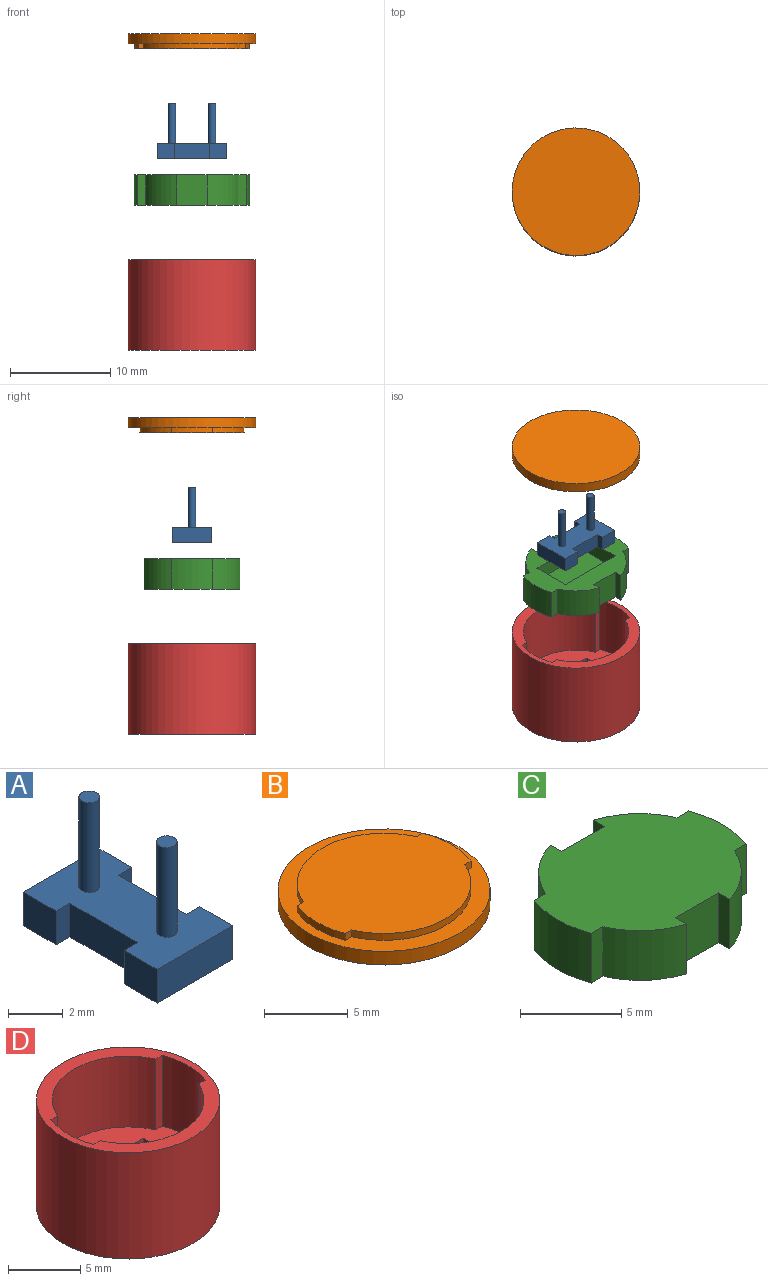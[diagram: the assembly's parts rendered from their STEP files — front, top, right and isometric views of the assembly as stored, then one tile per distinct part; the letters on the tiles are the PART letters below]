
ASSEMBLY  parts=4 mates=3
PART A: 18 faces, bbox 3.9x6.9x5.5 mm
  f0: plane 1.7x1.5mm, normal (1,0,0), area 2.5mm2, adj f2,f4,f7,f17
  f1: plane 1.7x1.5mm, normal (-1,0,0), area 2.5mm2, adj f2,f4,f7,f12
  f2: plane 6.9x3.9mm, normal (0,0,-1), area 22mm2, adj f0,f1,f3,f4,f5,f6,f12,f13
  f3: plane 1.7x1.5mm, normal (1,0,0), area 2.5mm2, adj f2,f6,f7,f15
  f4: plane 3.9x1.5mm, normal (0,1,0), area 5.9mm2, adj f0,f1,f2,f7
  f5: plane 1.7x1.5mm, normal (-1,0,0), area 2.5mm2, adj f2,f6,f7,f14
  f6: plane 3.9x1.5mm, normal (0,-1,0), area 5.9mm2, adj f2,f3,f5,f7
  f7: plane 6.9x3.9mm, normal (0,0,1), area 21.1mm2, adj f0,f1,f3,f4,f5,f6,f8,f10
  f8: cylinder r=0.38mm len=4mm, axis (0,0,-1), area 9.4mm2, adj f7,f9
  f9: plane 0.75x0.75mm, normal (0,0,1), area 0.4mm2, adj f8
  f10: cylinder r=0.38mm len=4mm, axis (0,0,-1), area 9.4mm2, adj f7,f11
  f11: plane 0.75x0.75mm, normal (0,0,1), area 0.4mm2, adj f10
  f12: plane 1.5x0.7mm, normal (0,-1,0), area 1.1mm2, adj f1,f2,f7,f13
  f13: plane 3.5x1.5mm, normal (-1,0,0), area 5.2mm2, adj f2,f7,f12,f14
  f14: plane 1.5x0.7mm, normal (0,1,0), area 1.1mm2, adj f2,f5,f7,f13
  f15: plane 1.5x0.7mm, normal (0,1,0), area 1.1mm2, adj f2,f3,f7,f16
  f16: plane 3.5x1.5mm, normal (1,0,0), area 5.2mm2, adj f2,f7,f15,f17
  f17: plane 1.5x0.7mm, normal (0,-1,0), area 1.1mm2, adj f0,f2,f7,f16
PART B: 12 faces, bbox 12.7x12.7x1.5 mm
  f0: cylinder r=6.35mm len=12.7mm, axis (0,0,1), area 39.9mm2, adj f1,f2
  f1: plane 12.7x12.7mm, normal (0,0,-1), area 126.7mm2, adj f0
  f2: plane 12.7x12.7mm, normal (0,0,1), area 37.5mm2, adj f0,f4,f5,f6,f7,f8,f9,f10
  f3: plane 11.4x10.4mm, normal (0,0,1), area 89.2mm2, adj f4,f5,f6,f7,f8,f9,f10,f11
  f4: plane 0.54x0.5mm, normal (0,1,0), area 0.3mm2, adj f2,f3,f6,f11
  f5: plane 0.54x0.5mm, normal (0,-1,0), area 0.3mm2, adj f2,f3,f6,f10
  f6: cylinder r=5.7mm len=4.1mm, axis (0,0,1), area 2.1mm2, adj f2,f3,f4,f5
  f7: plane 0.54x0.5mm, normal (0,-1,0), area 0.3mm2, adj f2,f3,f8,f10
  f8: cylinder r=5.7mm len=4.1mm, axis (0,0,1), area 2.1mm2, adj f2,f3,f7,f9
  f9: plane 0.54x0.5mm, normal (0,1,0), area 0.3mm2, adj f2,f3,f8,f11
  f10: cylinder r=5.2mm len=9.56mm, axis (0,0,1), area 6.1mm2, adj f2,f3,f5,f7
  f11: cylinder r=5.2mm len=9.56mm, axis (0,0,1), area 6.1mm2, adj f2,f3,f4,f9
PART C: 23 faces, bbox 11.5x9.5x3 mm
  f0: plane 11.5x9.54mm, normal (0,0,-1), area 51.1mm2, adj f1,f2,f4,f5,f6,f7,f8,f9
  f1: cylinder r=5mm len=3.08mm, axis (0,0,1), area 12.8mm2, adj f0,f3,f10,f18
  f2: cylinder r=5mm len=3.08mm, axis (0,0,1), area 12.8mm2, adj f0,f3,f8,f22
  f3: plane 11.5x9.54mm, normal (0,0,1), area 79.1mm2, adj f1,f2,f4,f5,f6,f7,f8,f9
  f4: cylinder r=5mm len=3.08mm, axis (0,0,1), area 12.8mm2, adj f0,f3,f7,f19
  f5: cylinder r=5mm len=3.08mm, axis (0,0,1), area 12.8mm2, adj f0,f3,f9,f20
  f6: cylinder r=5.75mm len=4mm, axis (0,0,1), area 12.3mm2, adj f0,f3,f7,f8
  f7: plane 3x0.81mm, normal (0,-1,0), area 2.4mm2, adj f0,f3,f4,f6
  f8: plane 3x0.81mm, normal (0,1,0), area 2.4mm2, adj f0,f2,f3,f6
  f9: plane 3x0.81mm, normal (0,1,0), area 2.4mm2, adj f0,f3,f5,f11
  f10: plane 3x0.81mm, normal (0,-1,0), area 2.4mm2, adj f0,f1,f3,f11
  f11: cylinder r=5.75mm len=4mm, axis (0,0,1), area 12.3mm2, adj f0,f3,f9,f10
  f12: plane 4x1.5mm, normal (-1,0,0), area 6mm2, adj f0,f13,f15,f16
  f13: plane 7x1.5mm, normal (0,1,0), area 10.5mm2, adj f0,f12,f14,f16
  f14: plane 4x1.5mm, normal (1,0,0), area 6mm2, adj f0,f13,f15,f16
  f15: plane 7x1.5mm, normal (0,-1,0), area 10.5mm2, adj f0,f12,f14,f16
  f16: plane 7x4mm, normal (0,0,-1), area 28mm2, adj f12,f13,f14,f15
  f17: plane 3x3mm, normal (0,-1,0), area 9mm2, adj f0,f3,f18,f19
  f18: plane 3x0.77mm, normal (-1,0,0), area 2.3mm2, adj f0,f1,f3,f17
  f19: plane 3x0.77mm, normal (1,0,0), area 2.3mm2, adj f0,f3,f4,f17
  f20: plane 3x0.77mm, normal (-1,0,0), area 2.3mm2, adj f0,f3,f5,f21
  f21: plane 3x3mm, normal (0,1,0), area 9mm2, adj f0,f3,f20,f22
  f22: plane 3x0.77mm, normal (1,0,0), area 2.3mm2, adj f0,f2,f3,f21
PART D: 17 faces, bbox 12.7x12.7x9 mm
  f0: plane 11.7x10.5mm, normal (0,0,1), area 63.8mm2, adj f1,f2,f6,f7,f8,f9,f10,f11
  f1: cylinder r=5.25mm len=9.62mm, axis (0,0,1), area 73mm2, adj f0,f4,f6,f9
  f2: cylinder r=5.25mm len=9.62mm, axis (0,0,1), area 73mm2, adj f0,f4,f8,f11
  f3: cylinder r=6.35mm len=12.7mm, axis (0,0,-1), area 359.1mm2, adj f4,f5
  f4: plane 12.7x12.7mm, normal (0,0,1), area 34.9mm2, adj f1,f2,f3,f6,f7,f8,f9,f10
  f5: plane 12.7x12.7mm, normal (0,0,-1), area 126.7mm2, adj f3
  f6: plane 6x0.65mm, normal (0,-1,0), area 3.9mm2, adj f0,f1,f4,f7
  f7: cylinder r=5.85mm len=6mm, axis (0,0,1), area 25.8mm2, adj f0,f4,f6,f8
  f8: plane 6x0.65mm, normal (0,1,0), area 3.9mm2, adj f0,f2,f4,f7
  f9: plane 6x0.65mm, normal (0,-1,0), area 3.9mm2, adj f0,f1,f4,f10
  f10: cylinder r=5.85mm len=6mm, axis (0,0,1), area 25.8mm2, adj f0,f4,f9,f11
  f11: plane 6x0.65mm, normal (0,1,0), area 3.9mm2, adj f0,f2,f4,f10
  f12: plane 4x1.5mm, normal (1,0,0), area 6mm2, adj f0,f13,f15,f16
  f13: plane 7x1.5mm, normal (0,1,0), area 10.5mm2, adj f0,f12,f14,f16
  f14: plane 4x1.5mm, normal (-1,0,0), area 6mm2, adj f0,f13,f15,f16
  f15: plane 7x1.5mm, normal (0,-1,0), area 10.5mm2, adj f0,f12,f14,f16
  f16: plane 7x4mm, normal (0,0,1), area 28mm2, adj f12,f13,f14,f15
PLACE A rot(axis=(0,0,-1),90deg) t=(-3.19,0.83,18.57)mm
PLACE B rot(axis=(1,0,0),180deg) t=(-3.19,0.83,30.5)mm
PLACE C rot(axis=(0,1,0),180deg) t=(-3.19,0.83,13.95)mm
PLACE D t=(-3.19,0.83,-0.5)mm fixed
MATE slider C.f6 <-> D.f2  axis (0,0,-1) through (-3.19,0.83,13.95)mm
MATE slider B.f0 <-> D.f3  axis (0,0,-1) through (-3.19,0.83,30)mm
MATE slider C.f11 <-> A.f2  axis (0,0,1) through (-3.19,0.83,15.45)mm
